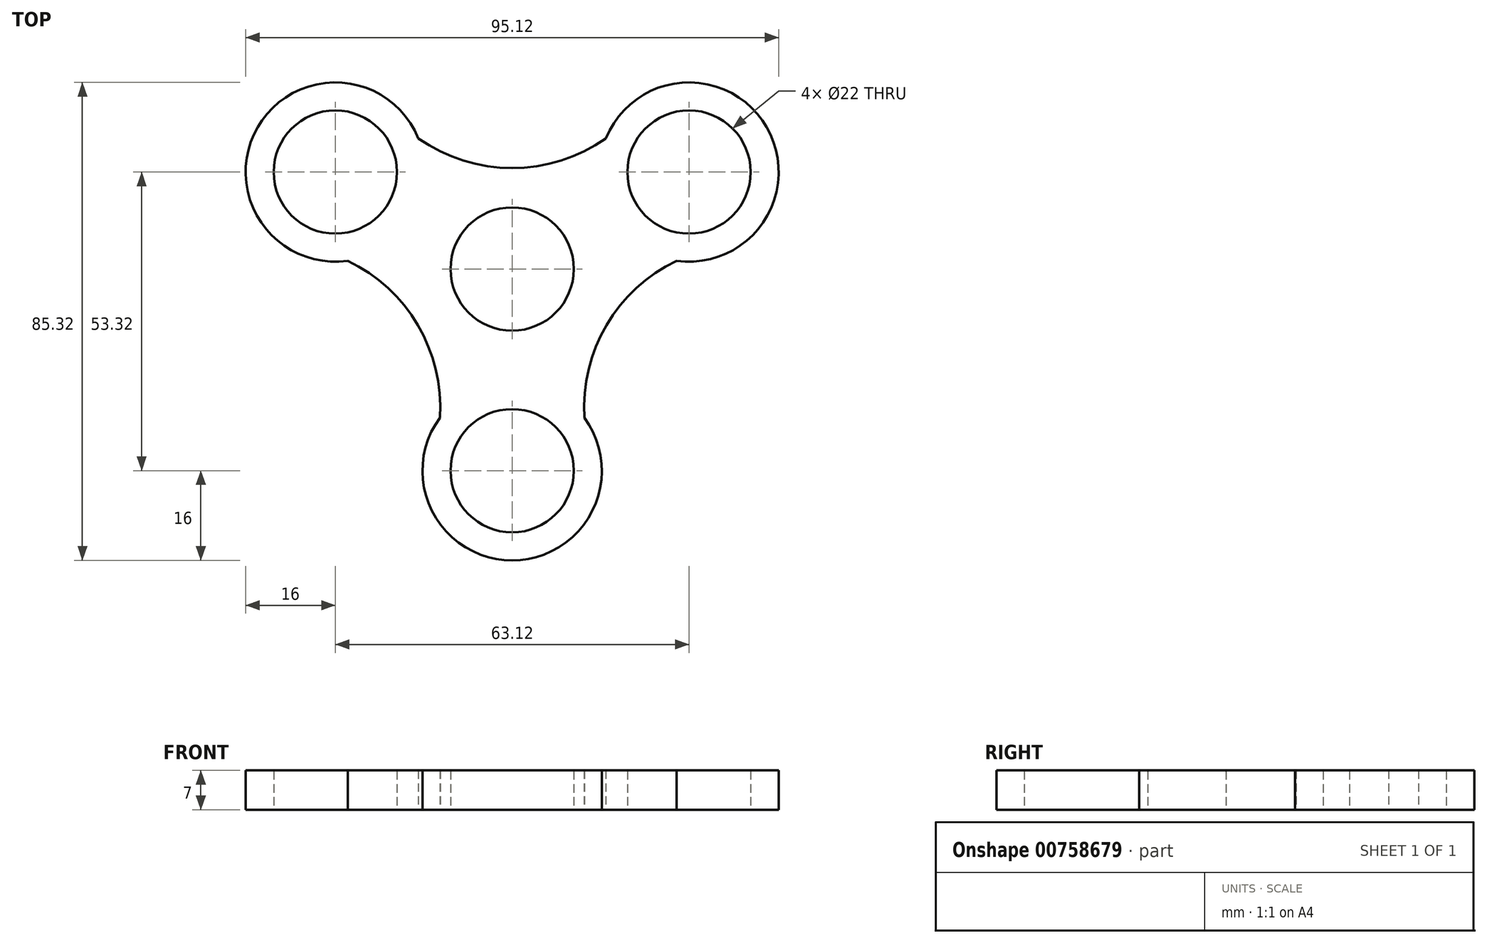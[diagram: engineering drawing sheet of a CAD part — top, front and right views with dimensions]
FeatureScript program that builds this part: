
annotation { "Feature Type Name" : "Feature", "Feature Type Description" : "" }
export const myFeature = defineFeature(function(context is Context, id is Id, definition is map)
    precondition{}
    {
        {
            var Q0;
            Q0=qCreatedBy(makeId("Top.planeOp"),FACE);
            var sketch = newSketch(context, id + "F0", { "sketchPlane" : qUnion([Q0])});
            skCircle(sketch, "E0", {"center": v(0, 0) * mm, "radius": 11 * mm});
            skCircle(sketch, "E1", {"center": v(-31.56, 17.32) * mm, "radius": 11 * mm});
            skCircle(sketch, "E2", {"center": v(31.56, 17.32) * mm, "radius": 11 * mm});
            skCircle(sketch, "E3", {"center": v(0, -36) * mm, "radius": 11 * mm});
            skLineSegment(sketch, "E4", {"start": v(0, 0) * mm, "end": v(0, -68.66) * mm, "construction": true});
            skCircle(sketch, "E5", {"center": v(31.56, 17.32) * mm, "radius": 16 * mm});
            skCircle(sketch, "E6", {"center": v(-31.56, 17.32) * mm, "radius": 16 * mm});
            skCircle(sketch, "E7", {"center": v(0, -36) * mm, "radius": 16 * mm});
            skLineSegment(sketch, "E8", {"start": v(-38.13, 2.73) * mm, "end": v(-31.56, 17.32) * mm, "construction": true});
            skLineSegment(sketch, "E9", {"start": v(-31.56, 17.32) * mm, "end": v(-24.99, 31.9) * mm, "construction": true});
            skPoint(sketch, "E10.orphan", {"position": v(24.99, 31.9) * mm});
            skLineSegment(sketch, "E11", {"start": v(38.13, 2.73) * mm, "end": v(31.56, 17.32) * mm, "construction": true});
            skLineSegment(sketch, "E12", {"start": v(31.56, 17.32) * mm, "end": v(24.99, 31.9) * mm, "construction": true});
            skLineSegment(sketch, "E13.trimOffspring", {"start": v(-38.13, 2.73) * mm, "end": v(-80.4, 3.52) * mm});
            skArc(sketch, "E14", {"start": v(29.35, 1.47) * mm, "mid": v(16.84, -10) * mm, "end": v(12.9, -26.53) * mm});
            skArc(sketch, "E15", {"start": v(-12.9, -26.53) * mm, "mid": v(-16.84, -10) * mm, "end": v(-29.35, 1.47) * mm});
            skLineSegment(sketch, "E16", {"start": v(29.35, 1.47) * mm, "end": v(-64.15, 1.47) * mm, "construction": true});
            skLineSegment(sketch, "E17", {"start": v(-29.35, 1.47) * mm, "end": v(0, 52.3) * mm, "construction": true});
            skLineSegment(sketch, "E18", {"start": v(0, 52.3) * mm, "end": v(29.35, 1.47) * mm, "construction": true});
            skArc(sketch, "E19", {"start": v(-16.73, 23.33) * mm, "mid": v(0, 18.02) * mm, "end": v(16.73, 23.33) * mm});
            skLineSegment(sketch, "E20", {"start": v(-16.73, 23.33) * mm, "end": v(16.73, 23.33) * mm, "construction": true});
            skSolve(sketch);
        }
        {
            var Q0;
            {var subQ0=sQuery(id+"F0.wireOp",EDGE,"0TSceduz-cEnI-4jYJ-D3ID-3SMpwCBie2t2");Q0=makeQuery(id+"F0.imprint","IMPRINT",FACE,{"disambiguationData":[TD([[makeQuery(id+"F0.imprint","IMPRINT",EDGE,{"derivedFrom":subQ0}),-1.0]])]});}
            var Q1;
            {var subQ0=sQuery(id+"F0.wireOp",EDGE,"e62Aefh6-yg1u-UyLL-kMEe-4k4CW6gHobVo");Q1=makeQuery(id+"F0.imprint","IMPRINT",FACE,{"disambiguationData":[TD([[makeQuery(id+"F0.imprint","IMPRINT",EDGE,{"derivedFrom":subQ0}),-1.0]])]});}
            var Q2;
            Q2=makeQuery(id+"F0.imprint","IMPRINT",FACE,{"disambiguationData":[TD([[makeQuery(id+"F0.imprint","IMPRINT",EDGE,{"derivedFrom":sQuery(id+"F0.wireOp",EDGE,"E0")}),-1.0]])]});
            extrude(context, id + "F1", {"entities" : qUnion([Q0, Q1, Q2]), "depth" : 7 * mm, "offsetDistance" : 25 * mm});
        }
        {
            var Q0;
            Q0=makeQuery(id+"F0.imprint","IMPRINT",FACE,{"disambiguationData":[TD([[makeQuery(id+"F0.imprint","IMPRINT",EDGE,{"derivedFrom":sQuery(id+"F0.wireOp",EDGE,"E2")}),-1.0]])]});
            var Q1;
            Q1=makeQuery(id+"F0.imprint","IMPRINT",FACE,{"disambiguationData":[TD([[makeQuery(id+"F0.imprint","IMPRINT",EDGE,{"derivedFrom":sQuery(id+"F0.wireOp",EDGE,"E1")}),-1.0]])]});
            var Q2;
            Q2=makeQuery(id+"F0.imprint","IMPRINT",FACE,{"disambiguationData":[TD([[makeQuery(id+"F0.imprint","IMPRINT",EDGE,{"derivedFrom":sQuery(id+"F0.wireOp",EDGE,"E3")}),-1.0]])]});
            extrude(context, id + "F2", {"entities" : qUnion([Q0, Q1, Q2]), "operationType" : NewBodyOperationType.ADD, "depth" : 7 * mm, "offsetDistance" : 25 * mm});
        }
        {
            var Q0;
            Q0=makeQuery(id+"F1.opExtrude","CAP_EDGE",EDGE,{"disambiguationData":[OSD([sQuery(id+"F0.wireOp",EDGE,"E0")])],"isStart":false});
            fillet(context, id + "F3", {"entities" : qUnion([Q0]), "radius" : 0.15 * mm, "tangentPropagation" : true, "allowEdgeOverflow" : false});
        }
        {
            var Q0;
            Q0=makeQuery(id+"F2.opExtrude","CAP_EDGE",EDGE,{"disambiguationData":[OSD([sQuery(id+"F0.wireOp",EDGE,"E1")])],"isStart":false});
            var Q1;
            Q1=makeQuery(id+"F2.opExtrude","CAP_EDGE",EDGE,{"disambiguationData":[OSD([sQuery(id+"F0.wireOp",EDGE,"E3")])],"isStart":false});
            fillet(context, id + "F4", {"entities" : qUnion([Q0, Q1]), "radius" : 0.15 * mm, "tangentPropagation" : true, "allowEdgeOverflow" : false});
        }
        {
            var Q0;
            Q0=makeQuery(id+"F2.opExtrude","CAP_EDGE",EDGE,{"disambiguationData":[OSD([sQuery(id+"F0.wireOp",EDGE,"E2")])],"isStart":false});
            fillet(context, id + "F5", {"entities" : qUnion([Q0]), "radius" : 0.15 * mm, "tangentPropagation" : true, "allowEdgeOverflow" : false});
        }
    });
